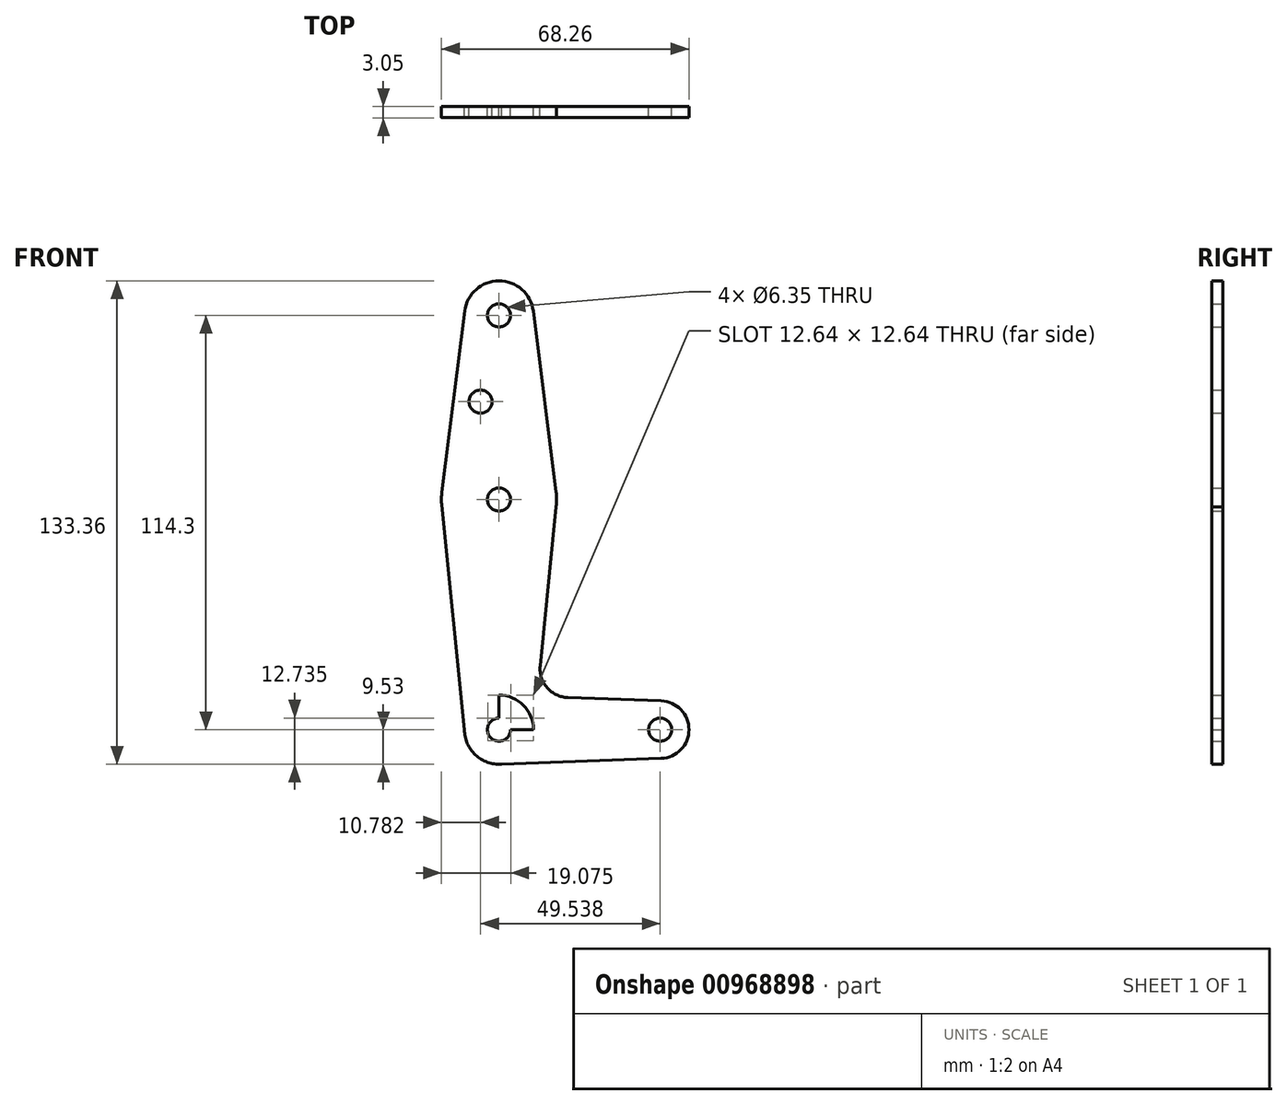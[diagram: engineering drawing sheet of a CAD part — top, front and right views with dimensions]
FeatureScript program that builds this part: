
annotation { "Feature Type Name" : "Feature", "Feature Type Description" : "" }
export const myFeature = defineFeature(function(context is Context, id is Id, definition is map)
    precondition{}
    {
        {
            var Q0;
            Q0=qCreatedBy(makeId("Front.planeOp"),FACE);
            var sketch = newSketch(context, id + "F0", { "sketchPlane" : qUnion([Q0])});
            skCircle(sketch, "E0", {"center": v(0, 114.3) * mm, "radius": 9.53 * mm});
            skLineSegment(sketch, "E1", {"start": v(0, 114.3) * mm, "end": v(0, 63.5) * mm});
            skCircle(sketch, "E2", {"center": v(0, 63.5) * mm, "radius": 15.88 * mm});
            skLineSegment(sketch, "E3", {"start": v(0, 63.5) * mm, "end": v(0, 0) * mm});
            skCircle(sketch, "E4", {"center": v(0, 0) * mm, "radius": 9.53 * mm});
            skLineSegment(sketch, "E5", {"start": v(0, 0) * mm, "end": v(44.45, 0) * mm});
            skCircle(sketch, "E6", {"center": v(44.45, 0) * mm, "radius": 7.94 * mm});
            skLineSegment(sketch, "E7", {"start": v(-9.45, 115.5) * mm, "end": v(-15.75, 65.48) * mm});
            skLineSegment(sketch, "E8", {"start": v(9.45, 115.5) * mm, "end": v(15.75, 65.48) * mm});
            skLineSegment(sketch, "E9", {"start": v(15.74, 61.47) * mm, "end": v(11.34, 17.59) * mm});
            skCircle(sketch, "E10", {"center": v(0, 114.3) * mm, "radius": 3.18 * mm});
            skCircle(sketch, "E11", {"center": v(-5.09, 90.49) * mm, "radius": 3.18 * mm});
            skPoint(sketch, "E11.centerSnap0", {"position": v(-12.6, 90.49) * mm});
            skCircle(sketch, "E12", {"center": v(0, 63.5) * mm, "radius": 3.18 * mm});
            skCircle(sketch, "E13", {"center": v(0, 0) * mm, "radius": 3.18 * mm});
            skCircle(sketch, "E14", {"center": v(44.45, 0) * mm, "radius": 3.18 * mm});
            skLineSegment(sketch, "E15", {"start": v(18.97, 8.85) * mm, "end": v(44.73, 7.93) * mm});
            skLineSegment(sketch, "E16", {"start": v(0, -9.53) * mm, "end": v(44.73, -7.93) * mm});
            skPoint(sketch, "E17.newPointA", {"position": v(0, 9.53) * mm});
            skPoint(sketch, "E17.newPointB", {"position": v(9.57, 0) * mm});
            skArc(sketch, "E17.filletArc", {"start": v(11.34, 17.59) * mm, "mid": v(13.26, 11.57) * mm, "end": v(18.97, 8.85) * mm});
            skLineSegment(sketch, "E18", {"start": v(-9.52, 0) * mm, "end": v(-15.8, 61.9) * mm});
            skSolve(sketch);
        }
        {
            var Q0;
            Q0 = qSketchRegion(id + "F0", true);
            extrude(context, id + "F1", {"entities" : qUnion([Q0]), "depth" : 3.05 * mm, "offsetDistance" : 25.4 * mm});
        }
    });
